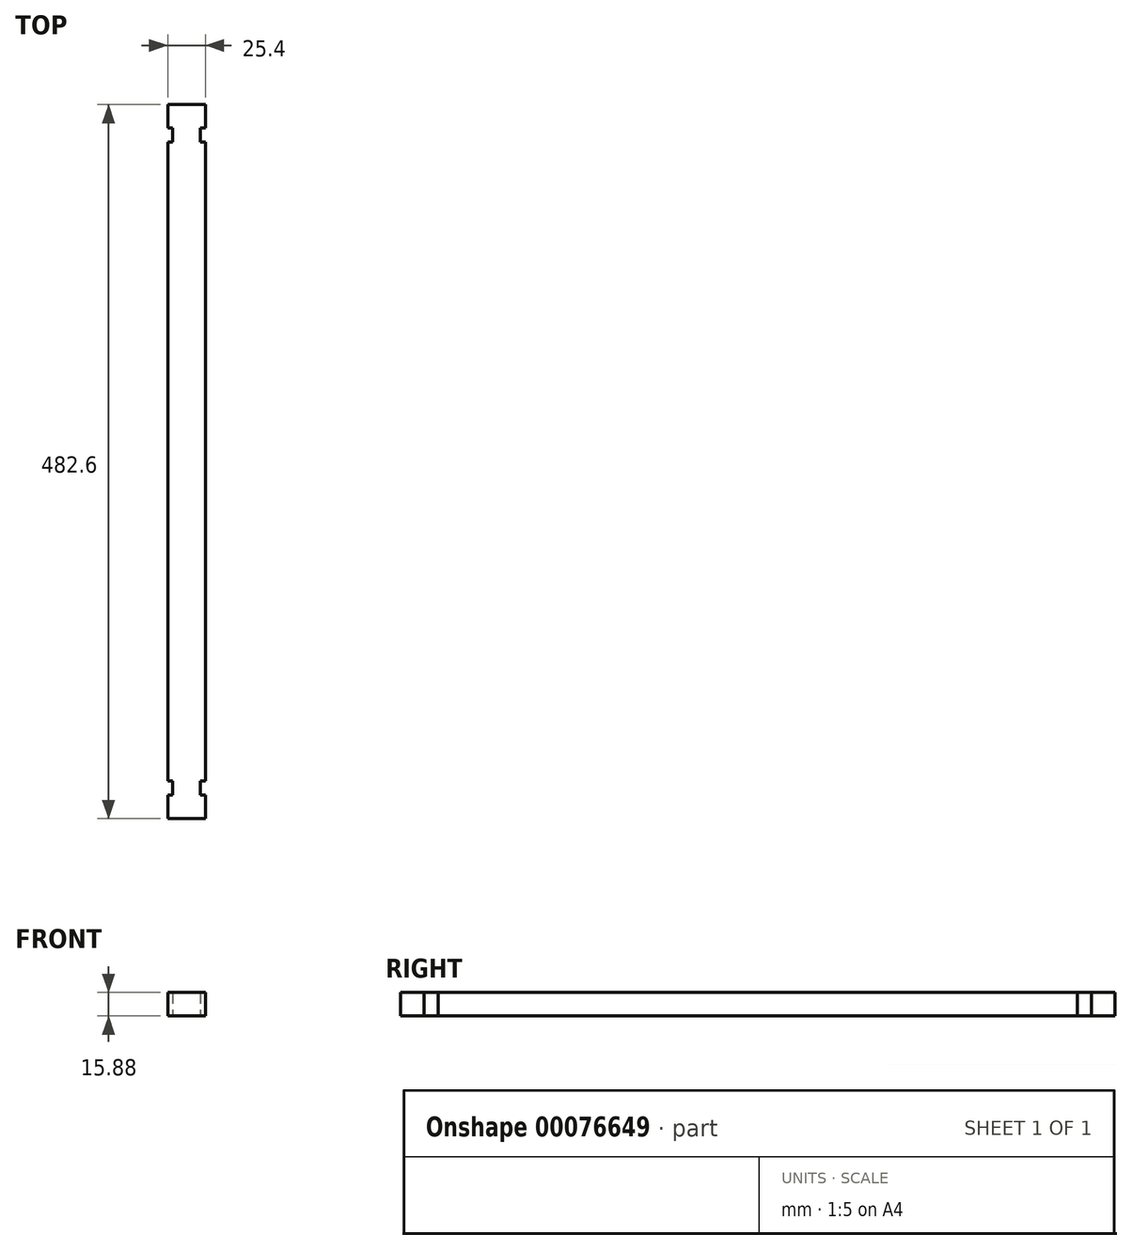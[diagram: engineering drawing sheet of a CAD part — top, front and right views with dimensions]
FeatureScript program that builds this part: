
annotation { "Feature Type Name" : "Feature", "Feature Type Description" : "" }
export const myFeature = defineFeature(function(context is Context, id is Id, definition is map)
    precondition{}
    {
        {
            var Q0;
            Q0=qCreatedBy(makeId("Top.planeOp"),FACE);
            var sketch = newSketch(context, id + "F0", { "sketchPlane" : qUnion([Q0])});
            skLineSegment(sketch, "E0.bottom", {"start": v(-14.5, 448.33) * mm, "end": v(10.9, 448.33) * mm});
            skLineSegment(sketch, "E0.top", {"start": v(-14.5, -34.27) * mm, "end": v(10.9, -34.27) * mm});
            skLineSegment(sketch, "E0.left", {"start": v(-14.5, 448.33) * mm, "end": v(-14.5, 432.46) * mm});
            skLineSegment(sketch, "E0.right", {"start": v(10.9, 448.33) * mm, "end": v(10.9, 432.46) * mm});
            skLineSegment(sketch, "E1.0", {"start": v(-14.5, 422.93) * mm, "end": v(-11.32, 422.93) * mm});
            skLineSegment(sketch, "E2.0", {"start": v(-14.5, 432.46) * mm, "end": v(-11.32, 432.46) * mm});
            skLineSegment(sketch, "E3", {"start": v(10.9, 432.46) * mm, "end": v(7.73, 432.46) * mm});
            skLineSegment(sketch, "E4", {"start": v(7.73, 432.46) * mm, "end": v(7.73, 422.93) * mm});
            skLineSegment(sketch, "E5", {"start": v(-11.32, 432.46) * mm, "end": v(-11.32, 422.93) * mm});
            skLineSegment(sketch, "E6", {"start": v(-11.32, 422.93) * mm, "end": v(-14.5, 422.93) * mm});
            skLineSegment(sketch, "E7.trimOffspring", {"start": v(7.73, 432.46) * mm, "end": v(10.9, 432.46) * mm});
            skLineSegment(sketch, "E8.trimOffspring", {"start": v(7.73, 422.93) * mm, "end": v(10.9, 422.93) * mm});
            skLineSegment(sketch, "E9.bottom", {"start": v(10.9, 432.46) * mm, "end": v(10.9, 432.46) * mm});
            skLineSegment(sketch, "E9.top", {"start": v(10.9, 422.93) * mm, "end": v(10.9, 422.93) * mm});
            skLineSegment(sketch, "E10.bottom", {"start": v(-14.5, 432.46) * mm, "end": v(-14.5, 432.46) * mm});
            skLineSegment(sketch, "E10.top", {"start": v(-14.5, 422.93) * mm, "end": v(-14.5, 422.93) * mm});
            skLineSegment(sketch, "E11.trimOffspring", {"start": v(10.9, 422.93) * mm, "end": v(10.9, -8.87) * mm});
            skLineSegment(sketch, "E12.trimOffspring", {"start": v(-14.5, 422.93) * mm, "end": v(-14.5, -8.87) * mm});
            skLineSegment(sketch, "E13.trimOffspring", {"start": v(-14.5, -18.4) * mm, "end": v(-14.5, -34.27) * mm});
            skLineSegment(sketch, "E14.trimOffspring", {"start": v(10.9, -18.4) * mm, "end": v(10.9, -34.27) * mm});
            skLineSegment(sketch, "E15", {"start": v(-11.32, -8.87) * mm, "end": v(-11.32, -18.4) * mm});
            skLineSegment(sketch, "E16", {"start": v(7.73, -8.87) * mm, "end": v(7.73, -18.4) * mm});
            skLineSegment(sketch, "E17", {"start": v(-14.5, -18.4) * mm, "end": v(-11.32, -18.4) * mm});
            skLineSegment(sketch, "E18", {"start": v(7.73, -18.4) * mm, "end": v(10.9, -18.4) * mm});
            skLineSegment(sketch, "E19", {"start": v(-11.32, -8.87) * mm, "end": v(-14.5, -8.87) * mm});
            skLineSegment(sketch, "E20", {"start": v(7.73, -8.87) * mm, "end": v(10.9, -8.87) * mm});
            skSolve(sketch);
        }
        {
            var Q0;
            Q0 = qSketchRegion(id + "F0", true);
            extrude(context, id + "F1", {"entities" : qUnion([Q0]), "depth" : 15.88 * mm});
        }
    });
